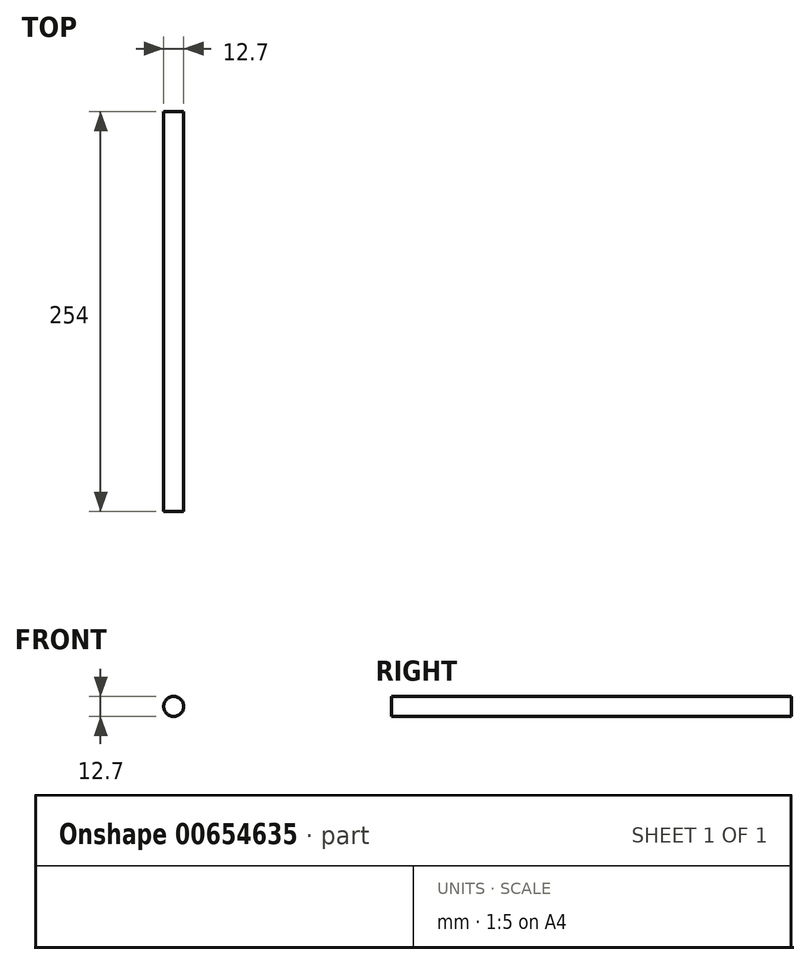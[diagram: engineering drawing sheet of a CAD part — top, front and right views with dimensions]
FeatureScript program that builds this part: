
annotation { "Feature Type Name" : "Feature", "Feature Type Description" : "" }
export const myFeature = defineFeature(function(context is Context, id is Id, definition is map)
    precondition{}
    {
        {
            var Q0;
            Q0=qCreatedBy(makeId("Front.planeOp"),FACE);
            var sketch = newSketch(context, id + "F0", { "sketchPlane" : qUnion([Q0])});
            skCircle(sketch, "E0", {"center": v(0, 0) * mm, "radius": 6.35 * mm});
            skSolve(sketch);
        }
        {
            var Q0;
            Q0=makeQuery(id+"F0.imprint","IMPRINT",FACE,{"disambiguationData":[TD([[makeQuery(id+"F0.imprint","IMPRINT",EDGE,{"derivedFrom":sQuery(id+"F0.wireOp",EDGE,"E0")}),1.0]])]});
            extrude(context, id + "F1", {"entities" : qUnion([Q0]), "depth" : 254 * mm, "offsetDistance" : 25.4 * mm});
        }
    });
